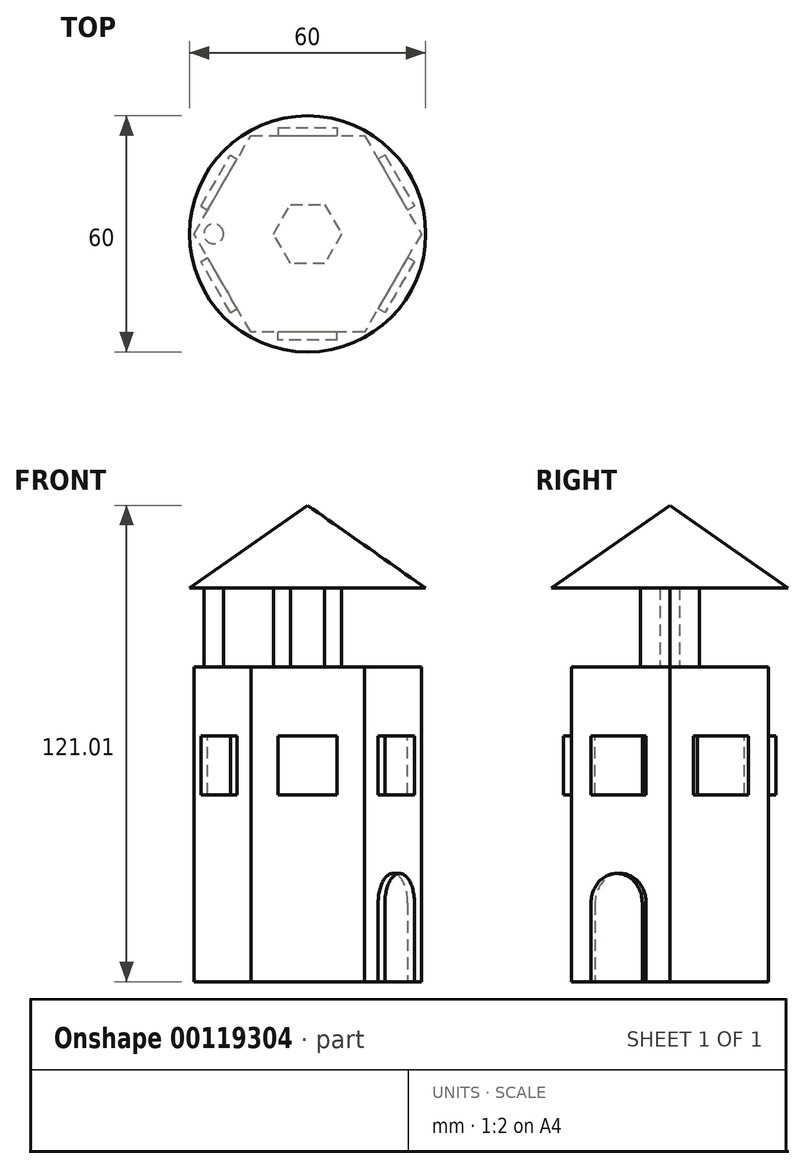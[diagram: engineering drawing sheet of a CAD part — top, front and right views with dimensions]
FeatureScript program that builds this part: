
annotation { "Feature Type Name" : "Feature", "Feature Type Description" : "" }
export const myFeature = defineFeature(function(context is Context, id is Id, definition is map)
    precondition{}
    {
        {
            var Q0;
            Q0=qCreatedBy(makeId("Top.planeOp"),FACE);
            var sketch = newSketch(context, id + "F0", { "sketchPlane" : qUnion([Q0])});
            skCircle(sketch, "E0.cCircle", {"center": v(0, 0) * mm, "radius": 25 * mm, "construction": true});
            skLineSegment(sketch, "E0.0", {"start": v(14.43, -25) * mm, "end": v(-14.43, -25) * mm});
            skLineSegment(sketch, "E0.1", {"start": v(-14.43, -25) * mm, "end": v(-28.87, 0) * mm});
            skLineSegment(sketch, "E0.2", {"start": v(-28.87, 0) * mm, "end": v(-14.43, 25) * mm});
            skLineSegment(sketch, "E0.3", {"start": v(-14.43, 25) * mm, "end": v(14.43, 25) * mm});
            skLineSegment(sketch, "E0.4", {"start": v(14.43, 25) * mm, "end": v(28.87, 0) * mm});
            skLineSegment(sketch, "E0.5", {"start": v(28.87, 0) * mm, "end": v(14.43, -25) * mm});
            skPoint(sketch, "E0.0.midPoint", {"position": v(0, -25) * mm});
            skSolve(sketch);
        }
        {
            var Q0;
            Q0=makeQuery(id+"F0.imprint","IMPRINT",FACE,{"disambiguationData":[TD([[makeQuery(id+"F0.imprint","IMPRINT",EDGE,{"derivedFrom":sQuery(id+"F0.wireOp",EDGE,"E0.0")}),-1.0]])]});
            extrude(context, id + "F1", {"entities" : qUnion([Q0]), "depth" : 80 * mm});
        }
        {
            var Q0;
            Q0=makeQuery(id+"F1.opExtrude","SWEPT_FACE",FACE,{"disambiguationData":[OSD([sQuery(id+"F0.wireOp",EDGE,"E0.0")])]});
            var sketch = newSketch(context, id + "F2", { "sketchPlane" : qUnion([Q0])});
            skLineSegment(sketch, "E1.bottom", {"start": v(7.5, 47.5) * mm, "end": v(-7.5, 47.5) * mm});
            skLineSegment(sketch, "E1.top", {"start": v(7.5, 62.5) * mm, "end": v(-7.5, 62.5) * mm});
            skLineSegment(sketch, "E1.left", {"start": v(7.5, 47.5) * mm, "end": v(7.5, 62.5) * mm});
            skLineSegment(sketch, "E1.right", {"start": v(-7.5, 47.5) * mm, "end": v(-7.5, 62.5) * mm});
            skPoint(sketch, "E1.middle", {"position": v(0, 55) * mm});
            skSolve(sketch);
        }
        {
            var Q0;
            Q0 = qSketchRegion(id + "F2", true);
            extrude(context, id + "F3", {"entities" : qUnion([Q0]), "depth" : 2 * mm});
        }
        {
            var Q0;
            Q0=makeQuery(id+"F1.opExtrude","CAP_FACE",FACE,{"disambiguationData":[OSD([sQuery(id+"F0.wireOp",EDGE,"E0.0"),sQuery(id+"F0.wireOp",EDGE,"E0.1"),sQuery(id+"F0.wireOp",EDGE,"E0.2"),sQuery(id+"F0.wireOp",EDGE,"E0.3"),sQuery(id+"F0.wireOp",EDGE,"E0.4"),sQuery(id+"F0.wireOp",EDGE,"E0.5")])],"isStart":false});
            var sketch = newSketch(context, id + "F4", { "sketchPlane" : qUnion([Q0])});
            skLineSegment(sketch, "E2", {"start": v(14.43, -25) * mm, "end": v(-14.43, 25) * mm, "construction": true});
            skCircle(sketch, "E3", {"center": v(0, 0) * mm, "radius": 13.31 * mm, "construction": true});
            skSolve(sketch);
        }
        {
            var Q0;
            Q0=makeQuery(id+"F3.opExtrude","SWEPT_BODY",BODY,{"disambiguationData":[OSD([sQuery(id+"F2.wireOp",EDGE,"E1.bottom"),sQuery(id+"F2.wireOp",EDGE,"E1.top"),sQuery(id+"F2.wireOp",EDGE,"E1.left"),sQuery(id+"F2.wireOp",EDGE,"E1.right")])]});
            var Q1;
            Q1=sQuery(id+"F4.wireOp",EDGE,"E3");
            circularPattern(context, id + "F5", {"entities" : qUnion([Q0]), "axis" : qUnion([Q1]), "angle" : 360 * degree, "instanceCount" : 6, "equalSpace" : true});
        }
        {
            var Q0;
            Q0=makeQuery(id+"F1.opExtrude","CAP_FACE",FACE,{"disambiguationData":[OSD([sQuery(id+"F0.wireOp",EDGE,"E0.0"),sQuery(id+"F0.wireOp",EDGE,"E0.1"),sQuery(id+"F0.wireOp",EDGE,"E0.2"),sQuery(id+"F0.wireOp",EDGE,"E0.3"),sQuery(id+"F0.wireOp",EDGE,"E0.4"),sQuery(id+"F0.wireOp",EDGE,"E0.5")])],"isStart":false});
            var sketch = newSketch(context, id + "F6", { "sketchPlane" : qUnion([Q0])});
            skLineSegment(sketch, "E4", {"start": v(-14.43, -25) * mm, "end": v(14.43, 25) * mm, "construction": true});
            skCircle(sketch, "E5", {"center": v(0, 0) * mm, "radius": 14.8 * mm, "construction": true});
            skCircle(sketch, "E6.cCircle", {"center": v(0, 0) * mm, "radius": 7.5 * mm, "construction": true});
            skLineSegment(sketch, "E6.0", {"start": v(4.33, -7.5) * mm, "end": v(-4.33, -7.5) * mm});
            skLineSegment(sketch, "E6.1", {"start": v(-4.33, -7.5) * mm, "end": v(-8.66, 0) * mm});
            skLineSegment(sketch, "E6.2", {"start": v(-8.66, 0) * mm, "end": v(-4.33, 7.5) * mm});
            skLineSegment(sketch, "E6.3", {"start": v(-4.33, 7.5) * mm, "end": v(4.33, 7.5) * mm});
            skLineSegment(sketch, "E6.4", {"start": v(4.33, 7.5) * mm, "end": v(8.66, 0) * mm});
            skLineSegment(sketch, "E6.5", {"start": v(8.66, 0) * mm, "end": v(4.33, -7.5) * mm});
            skPoint(sketch, "E6.0.midPoint", {"position": v(0, -7.5) * mm});
            skSolve(sketch);
        }
        {
            var Q0;
            Q0 = qSketchRegion(id + "F6", true);
            extrude(context, id + "F7", {"entities" : qUnion([Q0]), "depth" : 20 * mm});
        }
        {
            var Q0;
            Q0=makeQuery(id+"F1.opExtrude","CAP_FACE",FACE,{"disambiguationData":[OSD([sQuery(id+"F0.wireOp",EDGE,"E0.0"),sQuery(id+"F0.wireOp",EDGE,"E0.1"),sQuery(id+"F0.wireOp",EDGE,"E0.2"),sQuery(id+"F0.wireOp",EDGE,"E0.3"),sQuery(id+"F0.wireOp",EDGE,"E0.4"),sQuery(id+"F0.wireOp",EDGE,"E0.5")])],"isStart":false});
            var sketch = newSketch(context, id + "F8", { "sketchPlane" : qUnion([Q0])});
            skLineSegment(sketch, "E7", {"start": v(-28.87, 0) * mm, "end": v(28.87, 0) * mm, "construction": true});
            skCircle(sketch, "E8", {"center": v(0, 0) * mm, "radius": 12.77 * mm, "construction": true});
            skCircle(sketch, "E9", {"center": v(-23.87, 0) * mm, "radius": 2.5 * mm});
            skSolve(sketch);
        }
        {
            var Q0;
            Q0 = qSketchRegion(id + "F8", true);
            extrude(context, id + "F9", {"entities" : qUnion([Q0]), "operationType" : NewBodyOperationType.ADD, "depth" : 20 * mm});
        }
        {
            var Q0;
            Q0=makeQuery(id+"F1.opExtrude","CAP_FACE",FACE,{"disambiguationData":[OSD([sQuery(id+"F0.wireOp",EDGE,"E0.0"),sQuery(id+"F0.wireOp",EDGE,"E0.1"),sQuery(id+"F0.wireOp",EDGE,"E0.2"),sQuery(id+"F0.wireOp",EDGE,"E0.3"),sQuery(id+"F0.wireOp",EDGE,"E0.4"),sQuery(id+"F0.wireOp",EDGE,"E0.5")])],"isStart":false});
            var sketch = newSketch(context, id + "F10", { "sketchPlane" : qUnion([Q0])});
            skPoint(sketch, "E10", {"position": v(-14.43, -25) * mm});
            skLineSegment(sketch, "E11", {"start": v(-14.43, -25) * mm, "end": v(14.43, 25) * mm, "construction": true});
            skCircle(sketch, "E12", {"center": v(0, 0) * mm, "radius": 12.94 * mm, "construction": true});
            skSolve(sketch);
        }
        {
            var Q0;
            Q0=makeQuery(id+"F1.opExtrude","SWEPT_FACE",FACE,{"disambiguationData":[OSD([sQuery(id+"F0.wireOp",EDGE,"E0.5")])]});
            var sketch = newSketch(context, id + "F11", { "sketchPlane" : qUnion([Q0])});
            skArc(sketch, "E13", {"start": v(7.5, 20) * mm, "mid": v(0, 27.5) * mm, "end": v(-7.5, 20) * mm});
            skLineSegment(sketch, "E14", {"start": v(-7.5, 20) * mm, "end": v(-7.5, 0) * mm});
            skLineSegment(sketch, "E15", {"start": v(7.5, 20) * mm, "end": v(7.5, 0) * mm});
            skLineSegment(sketch, "E16", {"start": v(7.5, 0) * mm, "end": v(-7.5, 0) * mm});
            skSolve(sketch);
        }
        {
            var Q0;
            Q0=makeQuery(id+"F11.imprint","IMPRINT",FACE,{"disambiguationData":[TD([[makeQuery(id+"F11.imprint","IMPRINT",EDGE,{"derivedFrom":sQuery(id+"F11.wireOp",EDGE,"E13")}),1.0]])]});
            extrude(context, id + "F12", {"entities" : qUnion([Q0]), "depth" : 2 * mm});
        }
        {
            var Q0;
            Q0=makeQuery(id+"F7.opExtrude","CAP_FACE",FACE,{"disambiguationData":[OSD([sQuery(id+"F6.wireOp",EDGE,"E6.0"),sQuery(id+"F6.wireOp",EDGE,"E6.1"),sQuery(id+"F6.wireOp",EDGE,"E6.2"),sQuery(id+"F6.wireOp",EDGE,"E6.3"),sQuery(id+"F6.wireOp",EDGE,"E6.4"),sQuery(id+"F6.wireOp",EDGE,"E6.5")])],"isStart":false});
            var sketch = newSketch(context, id + "F13", { "sketchPlane" : qUnion([Q0])});
            skCircle(sketch, "E17", {"center": v(0, 0) * mm, "radius": 30 * mm});
            skSolve(sketch);
        }
        {
            var Q0;
            Q0 = qSketchRegion(id + "F13", true);
            extrude(context, id + "F14", {"entities" : qUnion([Q0]), "depth" : 25 * mm, "hasDraft" : true, "draftAngle" : 55 * degree, "draftPullDirection" : true});
        }
    });
